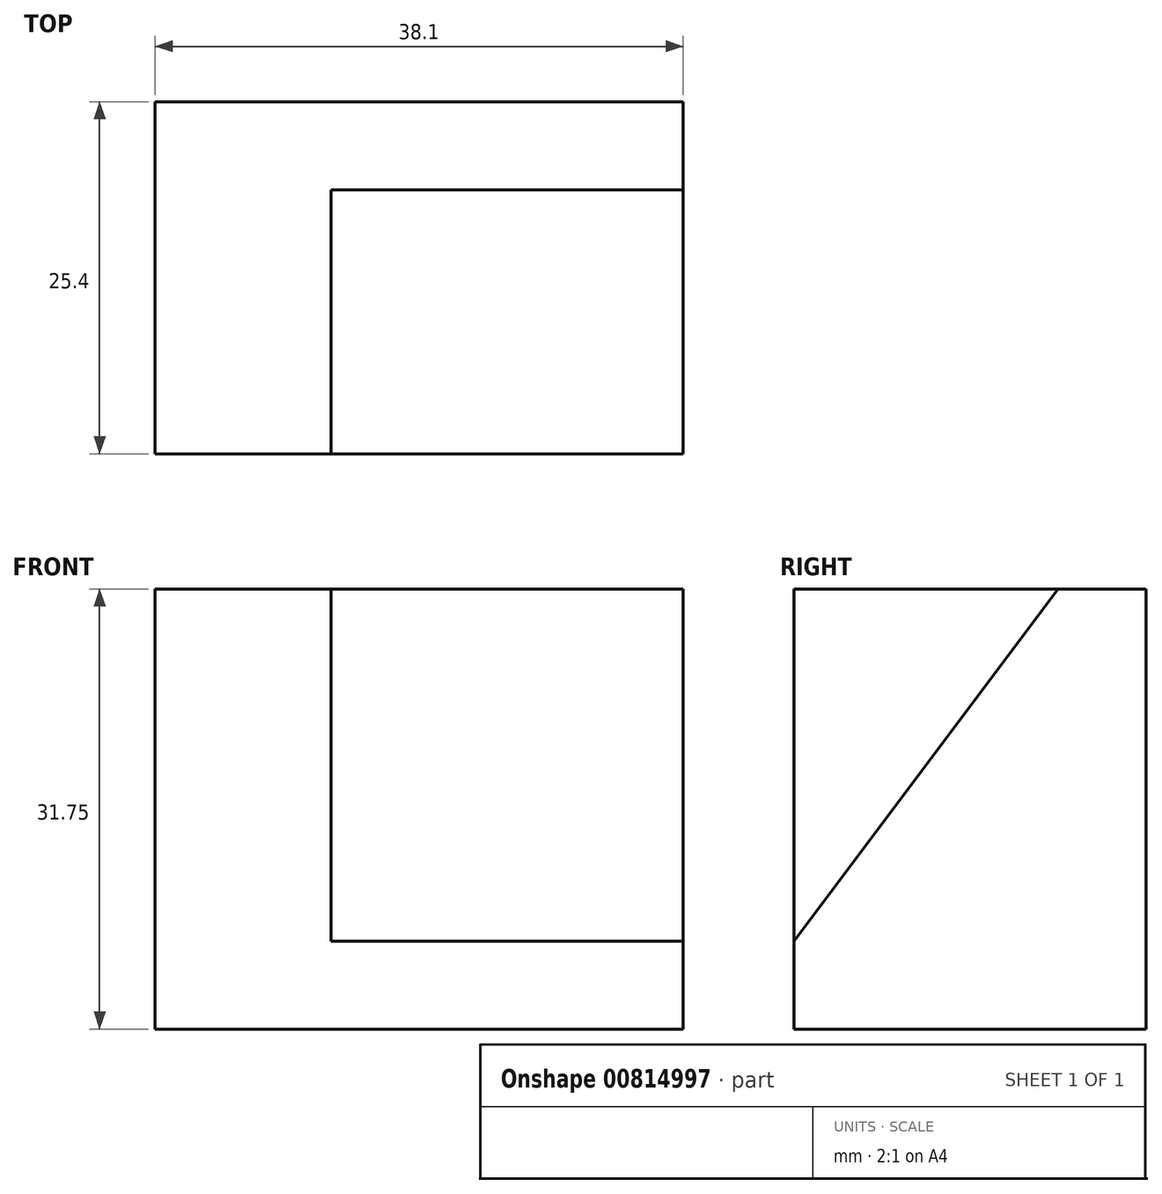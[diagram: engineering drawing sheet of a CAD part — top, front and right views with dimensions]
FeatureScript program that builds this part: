
annotation { "Feature Type Name" : "Feature", "Feature Type Description" : "" }
export const myFeature = defineFeature(function(context is Context, id is Id, definition is map)
    precondition{}
    {
        {
            var Q0;
            Q0=qCreatedBy(makeId("Right.planeOp"),FACE);
            var sketch = newSketch(context, id + "F0", { "sketchPlane" : qUnion([Q0])});
            skLineSegment(sketch, "E0", {"start": v(0, 0) * mm, "end": v(25.4, 0) * mm});
            skLineSegment(sketch, "E1", {"start": v(25.4, 0) * mm, "end": v(25.4, 31.75) * mm});
            skLineSegment(sketch, "E2", {"start": v(25.4, 31.75) * mm, "end": v(0, 31.75) * mm});
            skLineSegment(sketch, "E3", {"start": v(0, 31.75) * mm, "end": v(0, 0) * mm});
            skSolve(sketch);
        }
        {
            var Q0;
            Q0=makeQuery(id+"F0.imprint","IMPRINT",FACE,{"disambiguationData":[TD([[makeQuery(id+"F0.imprint","IMPRINT",EDGE,{"derivedFrom":sQuery(id+"F0.wireOp",EDGE,"E0")}),1.0]])]});
            extrude(context, id + "F1", {"entities" : qUnion([Q0]), "oppositeDirection" : true, "depth" : 38.1 * mm, "offsetDistance" : 25.4 * mm});
        }
        {
            var Q0;
            Q0=makeQuery(id+"F1.opExtrude","CAP_FACE",FACE,{"disambiguationData":[OSD([sQuery(id+"F0.wireOp",EDGE,"E0"),sQuery(id+"F0.wireOp",EDGE,"E1"),sQuery(id+"F0.wireOp",EDGE,"E2"),sQuery(id+"F0.wireOp",EDGE,"E3")])],"isStart":true});
            var sketch = newSketch(context, id + "F2", { "sketchPlane" : qUnion([Q0])});
            skLineSegment(sketch, "E4", {"start": v(25.4, 31.75) * mm, "end": v(19.05, 31.75) * mm});
            skLineSegment(sketch, "E5", {"start": v(0, 0) * mm, "end": v(0, 6.35) * mm});
            skLineSegment(sketch, "E6", {"start": v(0, 6.35) * mm, "end": v(19.05, 31.75) * mm});
            skSolve(sketch);
        }
        {
            var Q0;
            {var subQ0=sQuery(id+"F2.wireOp",EDGE,"E6");Q0=makeQuery(id+"F2.imprint","IMPRINT",FACE,{"disambiguationData":[TD([[makeQuery(id+"F2.imprint","IMPRINT",EDGE,{"derivedFrom":subQ0}),1.0]])]});}
            extrude(context, id + "F3", {"entities" : qUnion([Q0]), "operationType" : NewBodyOperationType.REMOVE, "oppositeDirection" : true, "depth" : 25.4 * mm, "offsetDistance" : 25.4 * mm});
        }
    });
